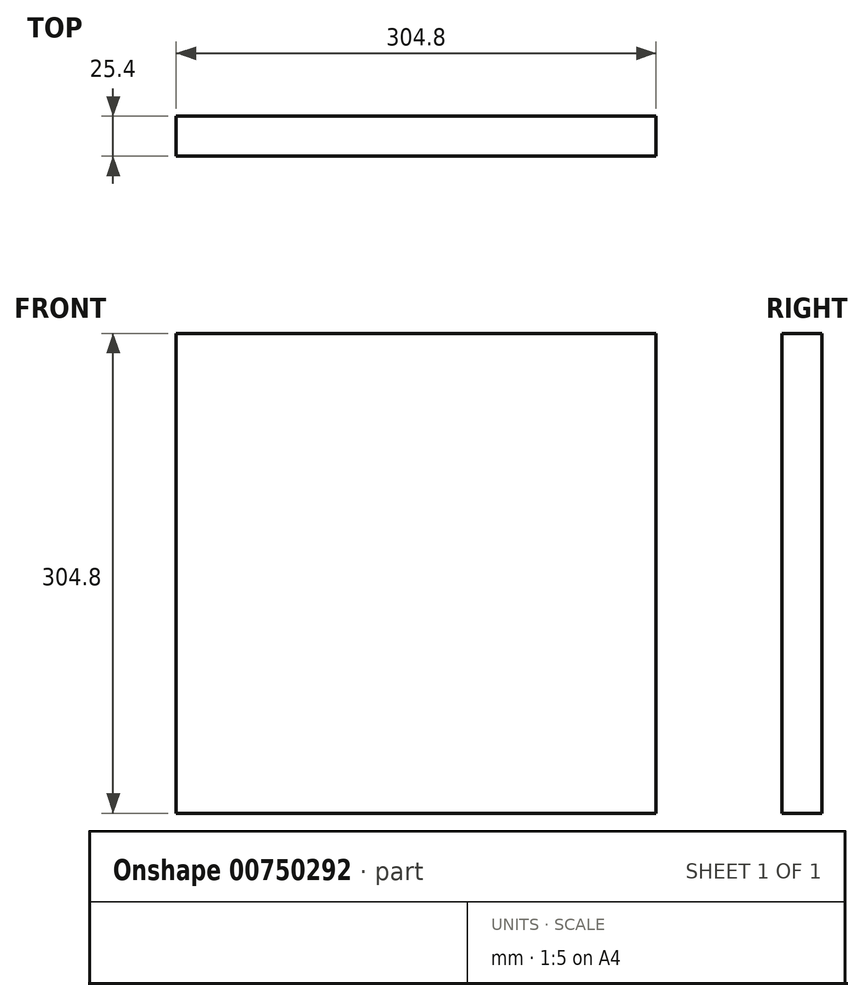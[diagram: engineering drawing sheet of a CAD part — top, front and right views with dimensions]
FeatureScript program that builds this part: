
annotation { "Feature Type Name" : "Feature", "Feature Type Description" : "" }
export const myFeature = defineFeature(function(context is Context, id is Id, definition is map)
    precondition{}
    {
        {
            var Q0;
            Q0=qCreatedBy(makeId("Front.planeOp"),FACE);
            var sketch = newSketch(context, id + "F0", { "sketchPlane" : qUnion([Q0])});
            skLineSegment(sketch, "E0.bottom", {"start": v(0, 0) * mm, "end": v(304.8, 0) * mm});
            skLineSegment(sketch, "E0.top", {"start": v(0, 304.8) * mm, "end": v(304.8, 304.8) * mm});
            skLineSegment(sketch, "E0.left", {"start": v(0, 0) * mm, "end": v(0, 304.8) * mm});
            skLineSegment(sketch, "E0.right", {"start": v(304.8, 0) * mm, "end": v(304.8, 304.8) * mm});
            skSolve(sketch);
        }
        {
            var Q0;
            Q0=makeQuery(id+"F0.imprint","IMPRINT",FACE,{"disambiguationData":[TD([[makeQuery(id+"F0.imprint","IMPRINT",EDGE,{"derivedFrom":sQuery(id+"F0.wireOp",EDGE,"E0.bottom")}),1.0]])]});
            extrude(context, id + "F1", {"entities" : qUnion([Q0]), "depth" : 25.4 * mm, "offsetDistance" : 25.4 * mm});
        }
    });
